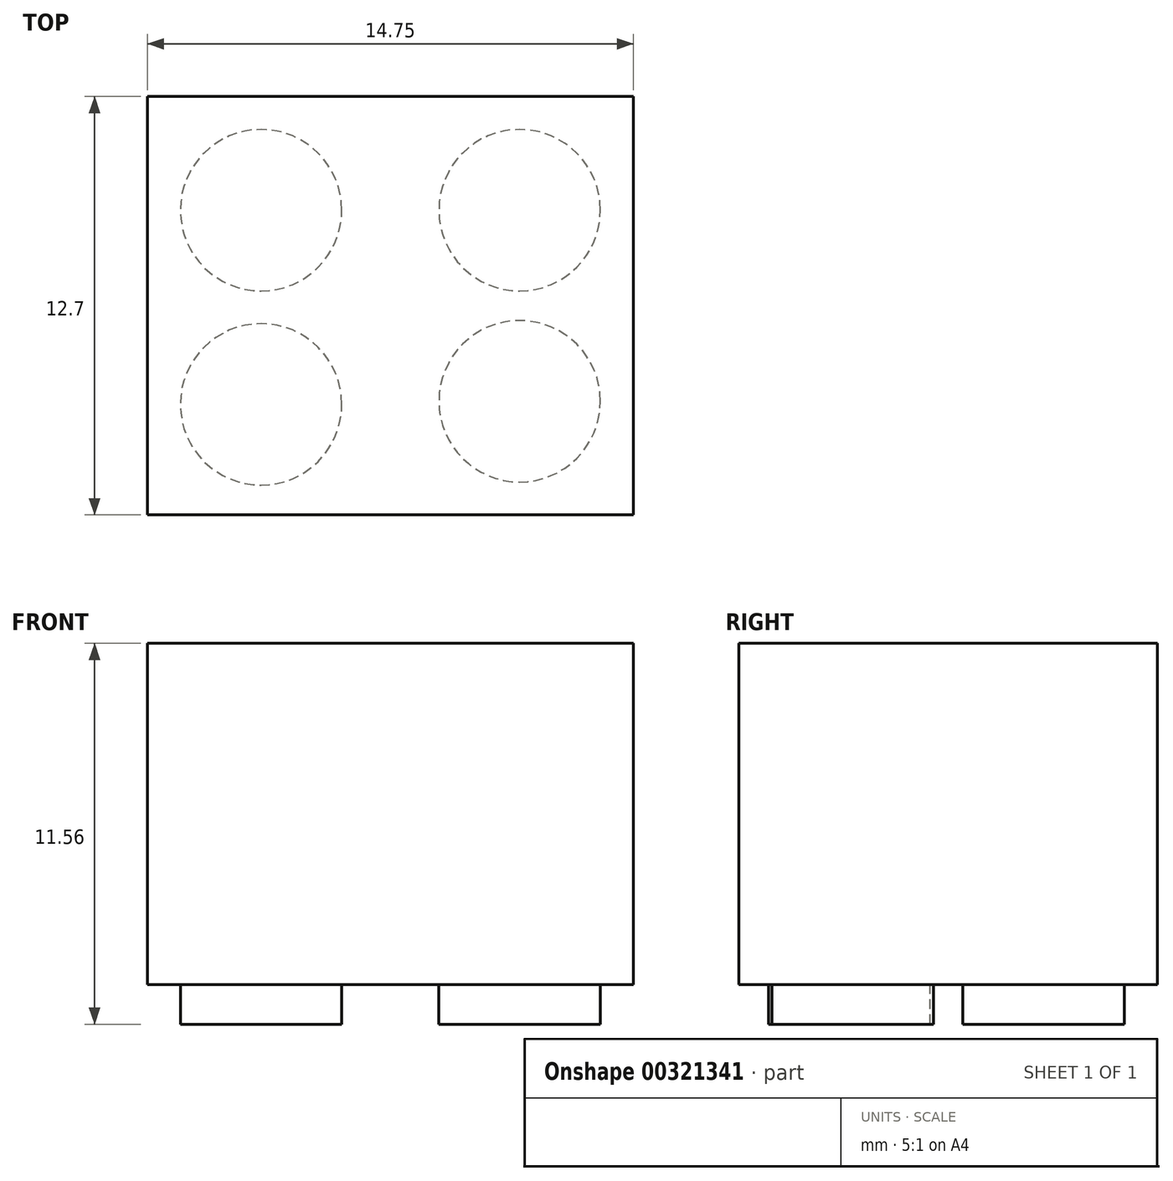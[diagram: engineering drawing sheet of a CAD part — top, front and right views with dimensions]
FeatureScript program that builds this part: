
annotation { "Feature Type Name" : "Feature", "Feature Type Description" : "" }
export const myFeature = defineFeature(function(context is Context, id is Id, definition is map)
    precondition{}
    {
        {
            var Q0;
            Q0=qCreatedBy(makeId("Front.planeOp"),FACE);
            var sketch = newSketch(context, id + "F0", { "sketchPlane" : qUnion([Q0])});
            skLineSegment(sketch, "E0", {"start": v(0, 0) * mm, "end": v(0, 10.36) * mm});
            skLineSegment(sketch, "E1", {"start": v(0, 10.36) * mm, "end": v(-14.75, 10.36) * mm});
            skLineSegment(sketch, "E2", {"start": v(-14.75, 10.36) * mm, "end": v(-14.75, 0) * mm});
            skLineSegment(sketch, "E3", {"start": v(-14.75, 0) * mm, "end": v(0, 0) * mm});
            skSolve(sketch);
        }
        {
            var Q0;
            Q0=makeQuery(id+"F0.imprint","IMPRINT",FACE,{"disambiguationData":[TD([[makeQuery(id+"F0.imprint","IMPRINT",EDGE,{"derivedFrom":sQuery(id+"F0.wireOp",EDGE,"E0")}),1.0]])]});
            extrude(context, id + "F1", {"entities" : qUnion([Q0]), "depth" : 12.7 * mm});
        }
        {
            var Q0;
            Q0=qCreatedBy(makeId("Top.planeOp"),FACE);
            var sketch = newSketch(context, id + "F2", { "sketchPlane" : qUnion([Q0])});
            skCircle(sketch, "E4", {"center": v(-3.45, -3.45) * mm, "radius": 2.45 * mm});
            skCircle(sketch, "E5", {"center": v(-11.3, -3.45) * mm, "radius": 2.45 * mm});
            skPoint(sketch, "E6.center.orphan", {"position": v(-13.75, -10.97) * mm});
            skCircle(sketch, "E7", {"center": v(-11.3, -9.35) * mm, "radius": 2.45 * mm});
            skPoint(sketch, "E8.center.orphan", {"position": v(-2.81, -10.97) * mm});
            skCircle(sketch, "E9", {"center": v(-3.45, -9.25) * mm, "radius": 2.45 * mm});
            skSolve(sketch);
        }
        {
            var Q0;
            Q0 = qSketchRegion(id + "F2", true);
            extrude(context, id + "F3", {"entities" : qUnion([Q0]), "operationType" : NewBodyOperationType.ADD, "oppositeDirection" : true, "depth" : 1.2 * mm});
        }
    });
